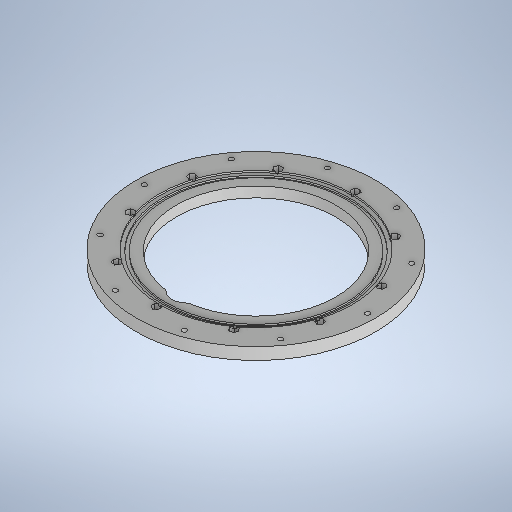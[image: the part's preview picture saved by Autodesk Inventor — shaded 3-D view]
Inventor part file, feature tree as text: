
AUTODESK INVENTOR PART (.ipt)
format: ipt  version: 2025.2 (Build 292293000, 293)  size: 600,576 bytes
history: native  units: in
note: dims shown in document units (in); Inventor stores cm internally (conversion verified against a paired STEP export)
features: sketch x12, extrude x6, plane x2, hole x1, revolve x1
ambient origin geometry x8: Origin, YZ Plane, XZ Plane, XY Plane, X Axis, Y Axis, Z Axis, Center Point
bodies: Solid1 (feature_tree)
feature tree (22):
  sketch  "Sketch1"  dims[d0=11.811in d1=7.874in]
  extrude  "Extrusion1"  Depth=7.874in
  sketch  "Sketch2"  dims[d7=0.2343in d9=3.937in d11=360.0deg]
  extrude  "Extrusion2"  Depth=0.1969in TaperAngle=0.0deg
  sketch  "Sketch3"  dims[d13=0.3012in d14=0.0in d15=9.8425in]
  extrude  "Extrusion3"  Depth=3.937in TaperAngle=360.0deg
  extrude  "Extrusion6"  Depth=9.8425in
  extrude  "Extrusion7"  Depth=0.1575in TaperAngle=0.0deg
  hole  "Hole2"  [1 undecoded]
  revolve  "Revolution1"  [1 undecoded]
  plane  "Work Plane3"
  plane  "Work Plane4"
  extrude  "Extrusion12"  Depth=0.1575in
  sketch  "Sketch Circular Pattern1"  dims[d2=9.8425in d5=0.1969in d6=0.0in]
  sketch  "Sketch5"  dims[d29=9.5079in d30=0.0837in d31=0.0in]
  sketch  "Sketch6"  dims[d47=3.937in d49=360.0deg]
  sketch  "Sketch8"  dims[d59=0.1575in]
  sketch  "Sketch Circular Pattern4"  dims[d20=0.1319in d21=0.0in d27=0.1575in d28=0.0in]
  sketch  "Sketch9"  dims[d60=0.5709in]
  sketch  "Sketch Circular Pattern5"  dims[d45=11.0236in d46=0.2165in]
  sketch  "Sketch Circular Pattern6"  dims[d51=0.2343in d52=0.2362in d53=0.4124in d54=0.2904in d55=90.0deg d56=0.315in d57=0.8108in d58=0.1575in]
  sketch  "Sketch13"  dims[d61=0.1575in d62=0.1575in d63=90.0deg d64=0.3445in d65=4.9213in d66=4.9213in d67=0.3445in d70=3.937in d72=360.0deg d74=3.937in d76=360.0deg d78=7.874in d79=7.874in d91=2.5in d92=1.5748in d93=3.2245in d94=10.0812in d95=0.0in d25=0.0197in d26=0.0344in]
note: 2 required parameter values undecoded (feature->parameter linkage not recoverable at this tier; creation-order binding heuristic only, values carry confidence <= 0.55)